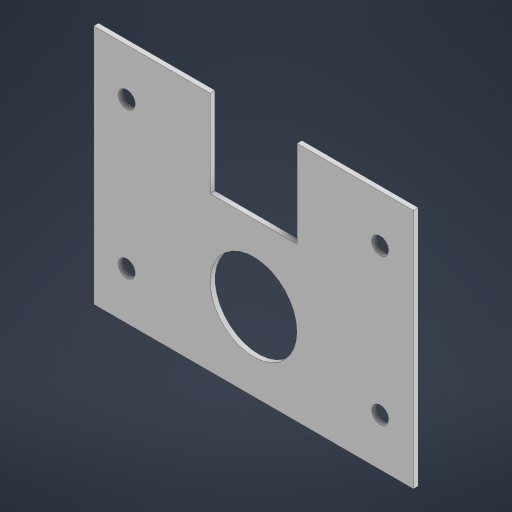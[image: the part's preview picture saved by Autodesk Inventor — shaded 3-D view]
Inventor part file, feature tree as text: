
AUTODESK INVENTOR PART (.ipt)
format: ipt  version: 2024 (Build 280153000, 153)  size: 187,904 bytes
history: native  units: in
note: dims shown in document units (in); Inventor stores cm internally (conversion verified against a paired STEP export)
features: sketch x2, extrude x1, hole x1, mirror x1
ambient origin geometry x8: Origin, YZ Plane, XZ Plane, XY Plane, X Axis, Y Axis, Z Axis, Center Point
bodies: Solid1 (feature_tree)
feature tree (5):
  extrude  "Extrusion1"  Depth=3.13in
  hole  "Hole1"  [1 undecoded]
  mirror  "Mirror1"
  sketch  "Sketch1"  dims[d0=4.15in d1=3.13in]
  sketch  "Sketch2"  dims[d2=1.13in d3=1.13in d4=1.01in d5=1.125in d6=0.0625in d7=0.0in d8=0.217in d9=0.75in d10=0.409in d11=0.25in d12=90.0deg d13=1.0in d14=0.8108in d15=1.9in d16=0.43in d17=0.43in d18=0.62in]
note: 1 required parameter value undecoded (feature->parameter linkage not recoverable at this tier; creation-order binding heuristic only, values carry confidence <= 0.55)
